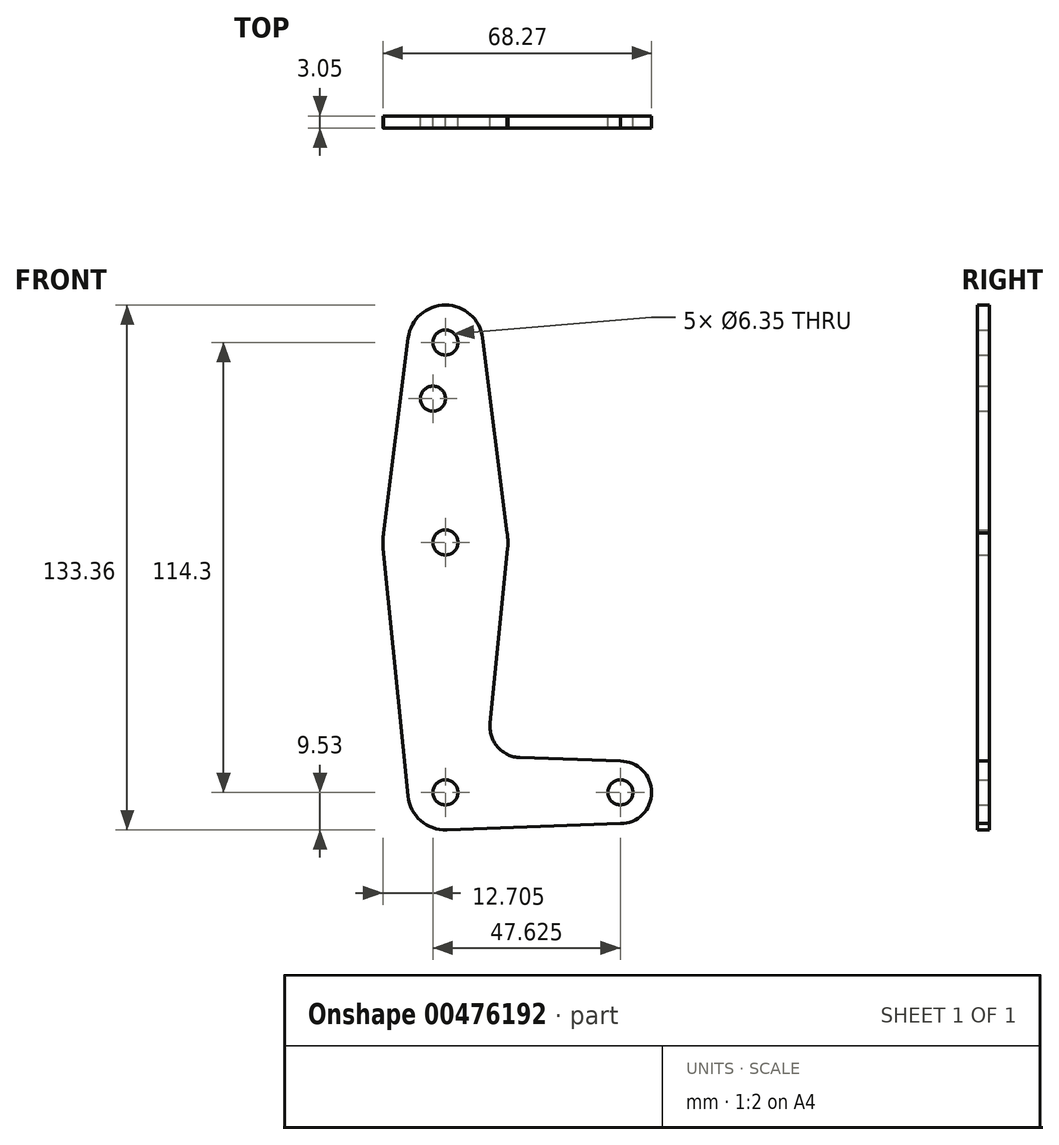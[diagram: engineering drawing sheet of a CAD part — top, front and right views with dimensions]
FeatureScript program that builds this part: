
annotation { "Feature Type Name" : "Feature", "Feature Type Description" : "" }
export const myFeature = defineFeature(function(context is Context, id is Id, definition is map)
    precondition{}
    {
        {
            var Q0;
            Q0=qCreatedBy(makeId("Front.planeOp"),FACE);
            var sketch = newSketch(context, id + "F0", { "sketchPlane" : qUnion([Q0])});
            skLineSegment(sketch, "E0", {"start": v(0, 0) * mm, "end": v(0, 63.5) * mm, "construction": true});
            skLineSegment(sketch, "E1", {"start": v(0, 63.5) * mm, "end": v(0, 114.3) * mm, "construction": true});
            skLineSegment(sketch, "E2", {"start": v(0, 0) * mm, "end": v(44.45, 0) * mm, "construction": true});
            skCircle(sketch, "E3", {"center": v(0, 114.3) * mm, "radius": 9.53 * mm});
            skCircle(sketch, "E4", {"center": v(0, 63.5) * mm, "radius": 15.88 * mm});
            skCircle(sketch, "E5", {"center": v(0, 0) * mm, "radius": 9.53 * mm});
            skCircle(sketch, "E6", {"center": v(44.45, 0) * mm, "radius": 7.94 * mm});
            skLineSegment(sketch, "E7", {"start": v(18.97, 8.85) * mm, "end": v(44.45, 7.94) * mm});
            skLineSegment(sketch, "E8", {"start": v(44.45, 7.94) * mm, "end": v(44.45, -7.94) * mm});
            skLineSegment(sketch, "E9", {"start": v(44.45, -7.94) * mm, "end": v(0, -9.53) * mm});
            skLineSegment(sketch, "E10", {"start": v(-15.8, 61.91) * mm, "end": v(-9.48, -0.95) * mm});
            skLineSegment(sketch, "E11", {"start": v(-15.8, 65.09) * mm, "end": v(-9.45, 115.49) * mm});
            skLineSegment(sketch, "E12", {"start": v(15.8, 65.09) * mm, "end": v(9.45, 115.49) * mm});
            skLineSegment(sketch, "E13", {"start": v(15.8, 61.91) * mm, "end": v(11.34, 17.59) * mm});
            skPoint(sketch, "E14.newPointA", {"position": v(9.48, -0.95) * mm});
            skArc(sketch, "E14.filletArc", {"start": v(11.34, 17.59) * mm, "mid": v(13.26, 11.57) * mm, "end": v(18.97, 8.85) * mm});
            skCircle(sketch, "E15", {"center": v(0, 114.3) * mm, "radius": 3.18 * mm});
            skCircle(sketch, "E16", {"center": v(0, 63.5) * mm, "radius": 3.18 * mm});
            skCircle(sketch, "E17", {"center": v(0, 0) * mm, "radius": 3.18 * mm});
            skCircle(sketch, "E18", {"center": v(44.45, 0) * mm, "radius": 3.18 * mm});
            skCircle(sketch, "E19", {"center": v(-3.18, 100.03) * mm, "radius": 3.18 * mm});
            skSolve(sketch);
        }
        {
            var Q0;
            Q0 = qSketchRegion(id + "F0", true);
            extrude(context, id + "F1", {"entities" : qUnion([Q0]), "depth" : 3.05 * mm});
        }
    });
